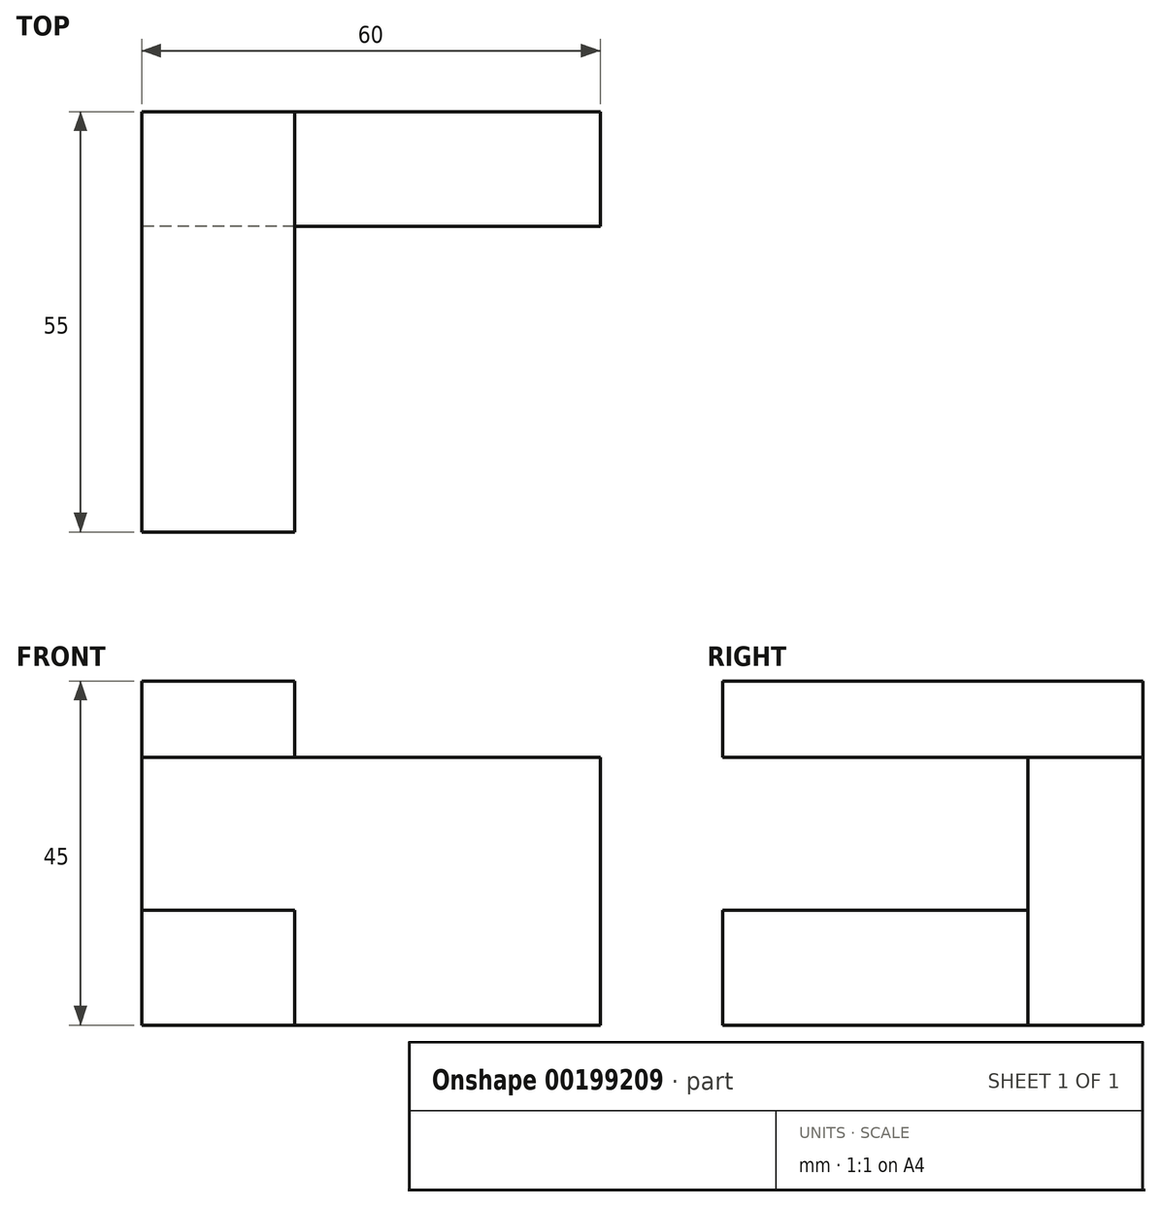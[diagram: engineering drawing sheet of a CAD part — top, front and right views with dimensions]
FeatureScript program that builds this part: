
annotation { "Feature Type Name" : "Feature", "Feature Type Description" : "" }
export const myFeature = defineFeature(function(context is Context, id is Id, definition is map)
    precondition{}
    {
        {
            var Q0;
            Q0=qCreatedBy(makeId("Right.planeOp"),FACE);
            var sketch = newSketch(context, id + "F0", { "sketchPlane" : qUnion([Q0])});
            skLineSegment(sketch, "E0.bottom", {"start": v(0, 0) * mm, "end": v(-55, 0) * mm});
            skLineSegment(sketch, "E0.top", {"start": v(0, 45) * mm, "end": v(-55, 45) * mm});
            skLineSegment(sketch, "E0.left", {"start": v(0, 0) * mm, "end": v(0, 45) * mm});
            skLineSegment(sketch, "E1", {"start": v(-15, 0) * mm, "end": v(-15, 27.87) * mm});
            skLineSegment(sketch, "E2", {"start": v(-15, 27.87) * mm, "end": v(0, 27.87) * mm});
            skLineSegment(sketch, "E3", {"start": v(-15, 27.87) * mm, "end": v(-15, 35) * mm});
            skLineSegment(sketch, "E4", {"start": v(-15, 35) * mm, "end": v(-55, 35) * mm});
            skLineSegment(sketch, "E5", {"start": v(-15, 15) * mm, "end": v(-55, 15) * mm});
            skLineSegment(sketch, "E6", {"start": v(-55, 0) * mm, "end": v(-55, 15) * mm});
            skLineSegment(sketch, "E7", {"start": v(-55, 35) * mm, "end": v(-55, 45) * mm});
            skSolve(sketch);
        }
        {
            var Q0;
            Q0 = qSketchRegion(id + "F0", true);
            extrude(context, id + "F1", {"entities" : qUnion([Q0]), "depth" : 60 * mm});
        }
        {
            var Q0;
            Q0=makeQuery(id+"F1.opExtrude","SWEPT_FACE",FACE,{"disambiguationData":[OSD([sQuery(id+"F0.wireOp",EDGE,"E0.top")])]});
            var sketch = newSketch(context, id + "F2", { "sketchPlane" : qUnion([Q0])});
            skLineSegment(sketch, "E8", {"start": v(20, -55) * mm, "end": v(20, 0) * mm});
            skLineSegment(sketch, "E9", {"start": v(20, -15) * mm, "end": v(60, -15) * mm});
            skSolve(sketch);
        }
        {
            var Q0;
            {var subQ4=sQuery(id+"F2.wireOp",EDGE,"E9");Q0=makeQuery(id+"F2.imprint","IMPRINT",FACE,{"disambiguationData":[TD([[makeQuery(id+"F2.imprint","IMPRINT",EDGE,{"derivedFrom":subQ4}),-1.0]])]});}
            extrude(context, id + "F3", {"entities" : qUnion([Q0]), "operationType" : NewBodyOperationType.REMOVE, "endBound" : BoundingType.THROUGH_ALL, "oppositeDirection" : true, "depth" : 25 * mm});
        }
        {
            var Q0;
            Q0=makeQuery(id+"F3.boolean.opBoolean","MERGE",FACE,{"derivedFrom":[makeQuery(id+"F1.opExtrude","SWEPT_FACE",FACE,{"disambiguationData":[OSD([sQuery(id+"F0.wireOp",EDGE,"E1"),sQuery(id+"F0.wireOp",EDGE,"E3")])]}),makeQuery(id+"F3.opExtrude","SWEPT_FACE",FACE,{"disambiguationData":[OSD([sQuery(id+"F2.wireOp",EDGE,"E9")])]})]});
            var sketch = newSketch(context, id + "F4", { "sketchPlane" : qUnion([Q0])});
            skLineSegment(sketch, "E10", {"start": v(20, 35) * mm, "end": v(60, 35) * mm});
            skSolve(sketch);
        }
        {
            var Q0;
            {var subQ0=sQuery(id+"F4.wireOp",EDGE,"E10");Q0=makeQuery(id+"F4.imprint","IMPRINT",FACE,{"disambiguationData":[TD([[makeQuery(id+"F4.imprint","IMPRINT",EDGE,{"derivedFrom":subQ0}),1.0]])]});}
            extrude(context, id + "F5", {"entities" : qUnion([Q0]), "operationType" : NewBodyOperationType.REMOVE, "oppositeDirection" : true, "depth" : 25 * mm});
        }
    });
